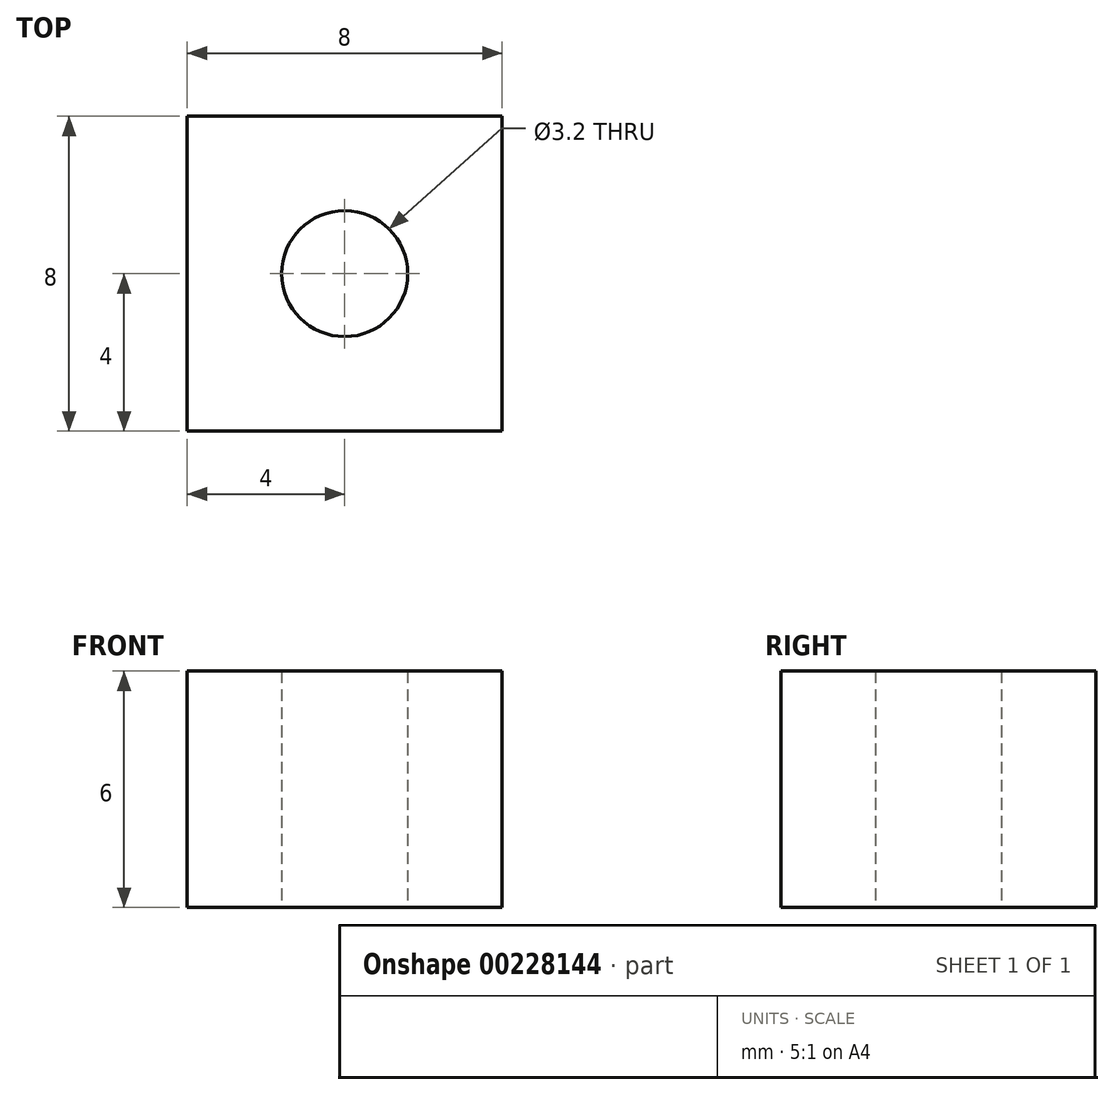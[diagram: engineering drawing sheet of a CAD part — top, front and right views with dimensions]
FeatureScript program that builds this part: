
annotation { "Feature Type Name" : "Feature", "Feature Type Description" : "" }
export const myFeature = defineFeature(function(context is Context, id is Id, definition is map)
    precondition{}
    {
        {
            var Q0;
            Q0=qCreatedBy(makeId("Top.planeOp"),FACE);
            var sketch = newSketch(context, id + "F0", { "sketchPlane" : qUnion([Q0])});
            skLineSegment(sketch, "E0.bottom", {"start": v(-4, 4) * mm, "end": v(4, 4) * mm});
            skLineSegment(sketch, "E0.top", {"start": v(-4, -4) * mm, "end": v(4, -4) * mm});
            skLineSegment(sketch, "E0.left", {"start": v(-4, 4) * mm, "end": v(-4, -4) * mm});
            skLineSegment(sketch, "E0.right", {"start": v(4, 4) * mm, "end": v(4, -4) * mm});
            skPoint(sketch, "E0.middle", {"position": v(0, 0) * mm});
            skCircle(sketch, "E1", {"center": v(0, 0) * mm, "radius": 1.6 * mm});
            skLineSegment(sketch, "E2.direction1", {"start": v(0, 0) * mm, "end": v(15, 0) * mm, "construction": true});
            skLineSegment(sketch, "E2.direction2", {"start": v(0, 0) * mm, "end": v(0, -15) * mm, "construction": true});
            skSolve(sketch);
        }
        {
            var Q0;
            Q0=makeQuery(id+"F0.imprint","IMPRINT",FACE,{"disambiguationData":[TD([[makeQuery(id+"F0.imprint","IMPRINT",EDGE,{"derivedFrom":sQuery(id+"F0.wireOp",EDGE,"E0.bottom")}),-1.0]])]});
            extrude(context, id + "F1", {"entities" : qUnion([Q0]), "depth" : 6 * mm});
        }
    });
